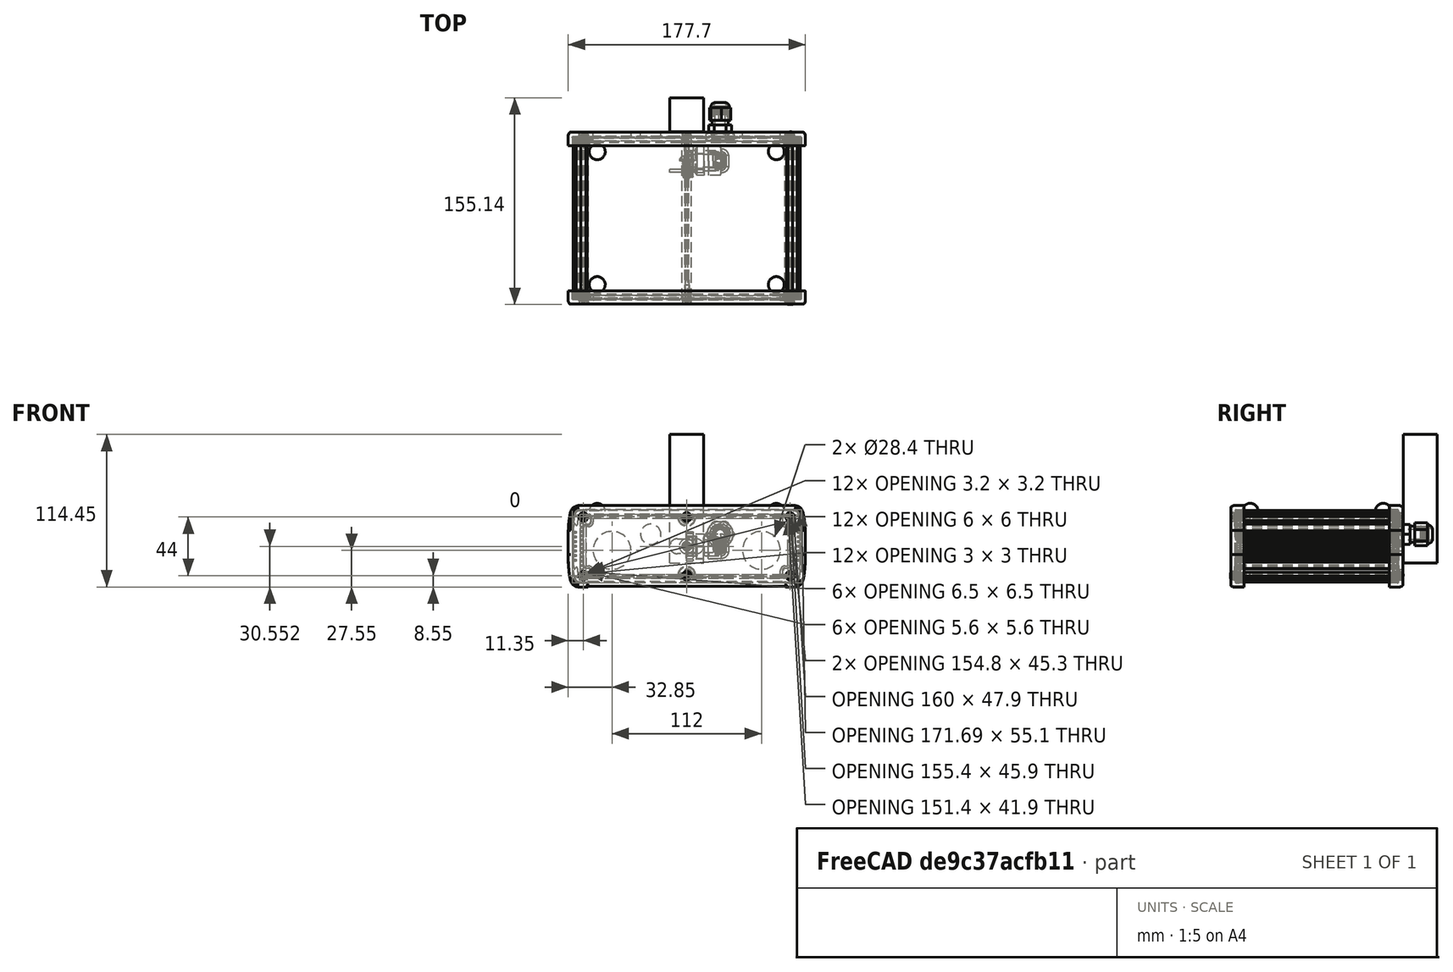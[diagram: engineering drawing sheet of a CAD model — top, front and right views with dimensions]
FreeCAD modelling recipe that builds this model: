
FCSTD DOCUMENT  (FreeCAD 0.19R24276 (Git))
Label: polyCaseCutOuts
License: All rights reserved
LicenseURL: http://en.wikipedia.org/wiki/All_rights_reserved
objects: Part::Feature×27, TechDraw::DrawViewDimension×25, Part::Cylinder×5, Part::Compound2×4, Part::Box×1, Part::MultiFuse×1, Part::Cut×1, TechDraw::DrawSVGTemplate×1, TechDraw::DrawViewPart×1, TechDraw::DrawPage×1
note: 35 computed .brp shape members not serialized (recipe doc carries the construction recipe); baked Part::Feature solids carry a one-line shape summary decoded from their .brp

FEATURE [Part::Feature] Feature  label="EX-64-002"
  Placement = pos=(0,-43,1e-14) rot=(0,0.707107,-0.707107;3.14159rad)
  shape: bbox 178.8 x 129.6 x 63.35 mm, 1628 faces, 33 solids (baked)
FEATURE [Part::Feature] Shell020
  shape: bbox 36.98 x 18.12 x 36.6 mm, 205 faces, 0 solids (baked)
FEATURE [Part::Feature] Shell021
  shape: bbox 36.98 x 21.68 x 36.68 mm, 152 faces, 0 solids (baked)
FEATURE [Part::Feature] Shell022
  shape: bbox 22.66 x 11.43 x 22.66 mm, 6 faces, 0 solids (baked)
FEATURE [Part::Feature] Shell023
  shape: bbox 24.46 x 14.2 x 24.46 mm, 102 faces, 0 solids (baked)
FEATURE [Part::Feature] Shell024
  shape: bbox 35.58 x 29.16 x 35.58 mm, 49 faces, 0 solids (baked)
FEATURE [Part::Feature] Shell025
  shape: bbox 0.2577 x 0.3048 x 0.4459 mm, 1 faces, 0 solids (baked)
FEATURE [Part::Feature] Shell026
  shape: bbox 0.3892 x 1.194 x 0.6742 mm, 1 faces, 0 solids (baked)
FEATURE [Part::Feature] Shell027
  shape: bbox 0.3612 x 0.889 x 0.6255 mm, 1 faces, 0 solids (baked)
FEATURE [Part::Feature] Shell028
  shape: bbox 0.2703 x 0.381 x 0.4682 mm, 1 faces, 0 solids (baked)
FEATURE [Part::Compound2] Compound001  label="M3222GBH_SW0001"
  Links = -> [Shell020,Shell021,Shell022,Shell023,Shell024,Shell025,Shell026,Shell027,Shell028]
  Placement = pos=(-56,9,-3) rot=(0,0,1;0rad)
FEATURE [Part::Feature] Solid003
  shape: bbox 15.45 x 36 x 21.9 mm, 27 faces (baked)
FEATURE [Part::Feature] Solid004
  shape: bbox 29.5 x 21.9 x 19 mm, 79 faces (baked)
FEATURE [Part::Feature] Solid002
  shape: bbox 1 x 19 x 19 mm, 6 faces (baked)
FEATURE [Part::Feature] Solid005
  shape: bbox 5.2 x 24 x 22.95 mm, 27 faces (baked)
FEATURE [Part::Feature] Solid001
  shape: bbox 8 x 12 x 12 mm, 6 faces (baked)
FEATURE [Part::Compound2] Compound002  label="PG9"
  Links = -> [Solid004,Solid001,Solid002,Solid003,Solid005]
  Placement = pos=(-27,14,9) rot=(0,0,1;1.5708rad)
FEATURE [Part::Box] Box  label="tSlotLog"
  AttacherType = Attacher::AttachEngine3D
  Height = 96.4
  Length = 25.4
  Placement = pos=(-12.7,22,-12.5) rot=(0,0,1;0rad)
  Width = 25.4
FEATURE [Part::Feature] Feature001  label="PG7"
  Placement = pos=(25,27,9) rot=(1,0,0;1.5708rad)
  shape: bbox 21.32 x 29.79 x 20.97 mm, 246 faces, 3 solids (baked)
FEATURE [Part::Feature] Shell029
  shape: bbox 36.98 x 21.68 x 36.68 mm, 152 faces, 0 solids (baked)
FEATURE [Part::Feature] Shell030
  shape: bbox 22.66 x 11.43 x 22.66 mm, 6 faces, 0 solids (baked)
FEATURE [Part::Feature] Shell031
  shape: bbox 0.3612 x 0.889 x 0.6255 mm, 1 faces, 0 solids (baked)
FEATURE [Part::Feature] Shell032
  shape: bbox 35.58 x 29.16 x 35.58 mm, 49 faces, 0 solids (baked)
FEATURE [Part::Feature] Shell033
  shape: bbox 24.46 x 14.2 x 24.46 mm, 102 faces, 0 solids (baked)
FEATURE [Part::Feature] Shell034
  shape: bbox 0.3892 x 1.194 x 0.6742 mm, 1 faces, 0 solids (baked)
FEATURE [Part::Feature] Shell035
  shape: bbox 0.2703 x 0.381 x 0.4682 mm, 1 faces, 0 solids (baked)
FEATURE [Part::Feature] Shell036
  shape: bbox 0.2577 x 0.3048 x 0.4459 mm, 1 faces, 0 solids (baked)
FEATURE [Part::Feature] Shell037
  shape: bbox 36.98 x 18.12 x 36.6 mm, 205 faces, 0 solids (baked)
FEATURE [Part::Compound2] Compound003  label="M3222GBH_SW0002"
  Links = -> [Shell037,Shell029,Shell030,Shell033,Shell032,Shell036,Shell034,Shell031,Shell035]
  Placement = pos=(56,9,-3) rot=(0,0,1;0rad)
FEATURE [Part::Feature] Solid
  shape: bbox 11.1 x 17.44 x 11.1 mm, 45 faces (baked)
FEATURE [Part::Feature] Solid006
  shape: bbox 25.4 x 3.15 x 11.25 mm, 11 faces (baked)
FEATURE [Part::Compound2] Compound  label="47065T139_T-Slotted Framing"
  Links = -> [Solid,Solid006]
  Placement = pos=(-2.4e-15,15,0) rot=(-0.707107,0,0.707107;3.14159rad)
FEATURE [Part::Cylinder] Cylinder  label="tSlotCut"
  Angle = 360
  AttacherType = Attacher::AttachEngine3D
  Height = 20
  Placement = pos=(0,9,0) rot=(-1,0,0;1.5708rad)
  Radius = 3.2
FEATURE [Part::Cylinder] Cylinder001  label="M3222GBH_SW0001_Cut"
  Angle = 360
  AttacherType = Attacher::AttachEngine3D
  Height = 50
  Placement = pos=(-56,-5,-3) rot=(-1,0,0;1.5708rad)
  Radius = 14.2
FEATURE [Part::Cylinder] Cylinder002  label="M3222GBH_SW0001_Cut001"
  Angle = 360
  AttacherType = Attacher::AttachEngine3D
  Height = 50
  Placement = pos=(56,-5,-3) rot=(-1,0,0;1.5708rad)
  Radius = 14.2
FEATURE [Part::Cylinder] Cylinder003  label="PG9Cut"
  Angle = 360
  AttacherType = Attacher::AttachEngine3D
  Height = 20
  Placement = pos=(-27,9,9) rot=(-1,0,0;1.5708rad)
  Radius = 7.6
FEATURE [Part::Cylinder] Cylinder004  label="PG9Cut001"
  Angle = 360
  AttacherType = Attacher::AttachEngine3D
  Height = 20
  Placement = pos=(25,9,9) rot=(-1,0,0;1.5708rad)
  Radius = 6.2
FEATURE [Part::MultiFuse] Fusion  label="cuts"
  Shapes = -> [Cylinder004,Cylinder003,Cylinder,Cylinder001,Cylinder002]
FEATURE [Part::Cut] Cut  label="Ex-64Cuts"
  Base = -> Feature
  Tool = -> Fusion
FEATURE [TechDraw::DrawSVGTemplate] Template
  EditableTexts = Designed_by_Name=Designed by Name; Drawing_number=Drawing number; FC-Date=Date; FC-SC=Scale; FC-SH=Sheet; FC-Title=Title; Subtitle=Subtitle; Weight=Weight
  Height = 210
  Orientation = 1
  Width = 297
FEATURE [TechDraw::DrawViewPart] View  label="External View"
  CoarseView = false
  Direction = (0,1,0)
  Focus = 100
  HardHidden = false
  IsoCount = 0
  IsoHidden = false
  IsoVisible = false
  LockPosition = false
  Perspective = false
  Rotation = 0
  ScaleType = 0
  SeamHidden = false
  SeamVisible = true
  SmoothHidden = false
  SmoothVisible = true
  Source = -> [Cut]
  X = 135.756
  XDirection = (-1,0,0)
  Y = 134.867
FEATURE [TechDraw::DrawViewDimension] Dimension002
  Arbitrary = false
  ArbitraryTolerances = false
  EqualTolerance = true
  FormatSpec = ⌀%.2f
  FormatSpecOverTolerance = %+.2f
  FormatSpecUnderTolerance = %+.2f
  Inverted = false
  LockPosition = false
  MeasureType = 1
  OverTolerance = 0
  References2D = -> [View]
  Rotation = 0
  ScaleType = 0
  TheoreticalExact = false
  Type = 5
  UnderTolerance = 0
  X = -26.8003
  Y = 11.2115
FEATURE [TechDraw::DrawViewDimension] Dimension001
  Arbitrary = false
  ArbitraryTolerances = false
  EqualTolerance = true
  FormatSpec = ⌀%.2f
  FormatSpecOverTolerance = %+.2f
  FormatSpecUnderTolerance = %+.2f
  Inverted = false
  LockPosition = false
  MeasureType = 1
  OverTolerance = 0
  References2D = -> [View]
  Rotation = 0
  ScaleType = 0
  TheoreticalExact = false
  Type = 5
  UnderTolerance = 0
  X = -53.3802
  Y = 0.342317
FEATURE [TechDraw::DrawViewDimension] Dimension
  Arbitrary = false
  ArbitraryTolerances = false
  EqualTolerance = true
  FormatSpec = %.2f
  FormatSpecOverTolerance = %+.2f
  FormatSpecUnderTolerance = %+.2f
  Inverted = false
  LockPosition = false
  MeasureType = 1
  OverTolerance = 0
  References2D = -> [View]
  Rotation = 0
  ScaleType = 0
  TheoreticalExact = false
  Type = 1
  UnderTolerance = 0
  X = 7.11e-14
  Y = -30.5235
FEATURE [TechDraw::DrawViewDimension] Dimension004
  Arbitrary = false
  ArbitraryTolerances = false
  EqualTolerance = true
  FormatSpec = ⌀%.2f
  FormatSpecOverTolerance = %+.2f
  FormatSpecUnderTolerance = %+.2f
  Inverted = false
  LockPosition = false
  MeasureType = 1
  OverTolerance = 0
  References2D = -> [View]
  Rotation = 0
  ScaleType = 0
  TheoreticalExact = false
  Type = 5
  UnderTolerance = 0
  X = 29.4596
  Y = 12.3737
FEATURE [TechDraw::DrawViewDimension] Dimension005
  Arbitrary = false
  ArbitraryTolerances = false
  EqualTolerance = true
  FormatSpec = ⌀%.2f
  FormatSpecOverTolerance = %+.2f
  FormatSpecUnderTolerance = %+.2f
  Inverted = false
  LockPosition = false
  MeasureType = 1
  OverTolerance = 0
  References2D = -> [View]
  Rotation = 0
  ScaleType = 0
  TheoreticalExact = false
  Type = 5
  UnderTolerance = 0
  X = 60.4786
  Y = 0.493887
FEATURE [TechDraw::DrawViewDimension] Dimension009
  Arbitrary = false
  ArbitraryTolerances = false
  EqualTolerance = true
  FormatSpec = %.2f
  FormatSpecOverTolerance = %+.2f
  FormatSpecUnderTolerance = %+.2f
  Inverted = false
  LockPosition = false
  MeasureType = 1
  OverTolerance = 0
  References2D = -> [View]
  Rotation = 0
  ScaleType = 0
  TheoreticalExact = false
  Type = 2
  UnderTolerance = 0
  X = -59.3059
  Y = 20.4711
FEATURE [TechDraw::DrawViewDimension] Dimension003
  Arbitrary = false
  ArbitraryTolerances = false
  EqualTolerance = true
  FormatSpec = ⌀%.2f
  FormatSpecOverTolerance = %+.2f
  FormatSpecUnderTolerance = %+.2f
  Inverted = false
  LockPosition = false
  MeasureType = 1
  OverTolerance = 0
  References2D = -> [View]
  Rotation = 0
  ScaleType = 0
  TheoreticalExact = false
  Type = 5
  UnderTolerance = 0
  X = 8.56795
  Y = 3.56177
FEATURE [TechDraw::DrawViewDimension] Dimension010
  Arbitrary = false
  ArbitraryTolerances = false
  EqualTolerance = true
  FormatSpec = %.2f
  FormatSpecOverTolerance = %+.2f
  FormatSpecUnderTolerance = %+.2f
  Inverted = false
  LockPosition = false
  MeasureType = 1
  OverTolerance = 0
  References2D = -> [View]
  Rotation = 0
  ScaleType = 0
  TheoreticalExact = false
  Type = 1
  UnderTolerance = 0
  X = -79.7934
  Y = 0.297386
FEATURE [TechDraw::DrawViewDimension] Dimension011
  Arbitrary = false
  ArbitraryTolerances = false
  EqualTolerance = true
  FormatSpec = %.2f
  FormatSpecOverTolerance = %+.2f
  FormatSpecUnderTolerance = %+.2f
  Inverted = false
  LockPosition = false
  MeasureType = 1
  OverTolerance = 0
  References2D = -> [View]
  Rotation = 0
  ScaleType = 0
  TheoreticalExact = false
  Type = 2
  UnderTolerance = 0
  X = -57.5045
  Y = -22.196
FEATURE [TechDraw::DrawViewDimension] Dimension012
  Arbitrary = false
  ArbitraryTolerances = false
  EqualTolerance = true
  FormatSpec = %.2f
  FormatSpecOverTolerance = %+.2f
  FormatSpecUnderTolerance = %+.2f
  Inverted = false
  LockPosition = false
  MeasureType = 1
  OverTolerance = 0
  References2D = -> [View]
  Rotation = 0
  ScaleType = 0
  TheoreticalExact = false
  Type = 2
  UnderTolerance = 0
  X = -26.9248
  Y = 24.0346
FEATURE [TechDraw::DrawViewDimension] Dimension013
  Arbitrary = false
  ArbitraryTolerances = false
  EqualTolerance = true
  FormatSpec = %.2f
  FormatSpecOverTolerance = %+.2f
  FormatSpecUnderTolerance = %+.2f
  Inverted = false
  LockPosition = false
  MeasureType = 1
  OverTolerance = 0
  References2D = -> [View]
  Rotation = 0
  ScaleType = 0
  TheoreticalExact = false
  Type = 2
  UnderTolerance = 0
  X = 22.4977
  Y = 25.2623
FEATURE [TechDraw::DrawViewDimension] Dimension014
  Arbitrary = false
  ArbitraryTolerances = false
  EqualTolerance = true
  FormatSpec = %.2f
  FormatSpecOverTolerance = %+.2f
  FormatSpecUnderTolerance = %+.2f
  Inverted = false
  LockPosition = false
  MeasureType = 1
  OverTolerance = 0
  References2D = -> [View]
  Rotation = 0
  ScaleType = 0
  TheoreticalExact = false
  Type = 2
  UnderTolerance = 0
  X = 52.8053
  Y = 21.0418
FEATURE [TechDraw::DrawViewDimension] Dimension015
  Arbitrary = false
  ArbitraryTolerances = false
  EqualTolerance = true
  FormatSpec = %.2f
  FormatSpecOverTolerance = %+.2f
  FormatSpecUnderTolerance = %+.2f
  Inverted = false
  LockPosition = false
  MeasureType = 1
  OverTolerance = 0
  References2D = -> [View]
  Rotation = 0
  ScaleType = 0
  TheoreticalExact = false
  Type = 1
  UnderTolerance = 0
  X = 78.3597
  Y = 2.50131
FEATURE [TechDraw::DrawViewDimension] Dimension016
  Arbitrary = false
  ArbitraryTolerances = false
  EqualTolerance = true
  FormatSpec = %.2f
  FormatSpecOverTolerance = %+.2f
  FormatSpecUnderTolerance = %+.2f
  Inverted = false
  LockPosition = false
  MeasureType = 1
  OverTolerance = 0
  References2D = -> [View]
  Rotation = 0
  ScaleType = 0
  TheoreticalExact = false
  Type = 2
  UnderTolerance = 0
  X = 53.3164
  Y = -21.4677
FEATURE [TechDraw::DrawViewDimension] Dimension017
  Arbitrary = false
  ArbitraryTolerances = false
  EqualTolerance = true
  FormatSpec = %.2f
  FormatSpecOverTolerance = %+.2f
  FormatSpecUnderTolerance = %+.2f
  Inverted = false
  LockPosition = false
  MeasureType = 1
  OverTolerance = 0
  References2D = -> [View]
  Rotation = 0
  ScaleType = 0
  TheoreticalExact = false
  Type = 1
  UnderTolerance = 0
  X = -60.9532
  Y = 5.48366
FEATURE [TechDraw::DrawViewDimension] Dimension018
  Arbitrary = false
  ArbitraryTolerances = false
  EqualTolerance = true
  FormatSpec = %.2f
  FormatSpecOverTolerance = %+.2f
  FormatSpecUnderTolerance = %+.2f
  Inverted = false
  LockPosition = false
  MeasureType = 1
  OverTolerance = 0
  References2D = -> [View]
  Rotation = 0
  ScaleType = 0
  TheoreticalExact = false
  Type = 1
  UnderTolerance = 0
  X = 17.0933
  Y = -2.49522
FEATURE [TechDraw::DrawViewDimension] Dimension019
  Arbitrary = false
  ArbitraryTolerances = false
  EqualTolerance = true
  FormatSpec = %.2f
  FormatSpecOverTolerance = %+.2f
  FormatSpecUnderTolerance = %+.2f
  Inverted = false
  LockPosition = false
  MeasureType = 1
  OverTolerance = 0
  References2D = -> [View]
  Rotation = 0
  ScaleType = 0
  TheoreticalExact = false
  Type = 2
  UnderTolerance = 0
  X = -28.1319
  Y = -12.4515
FEATURE [TechDraw::DrawViewDimension] Dimension020
  Arbitrary = false
  ArbitraryTolerances = false
  EqualTolerance = true
  FormatSpec = %.2f
  FormatSpecOverTolerance = %+.2f
  FormatSpecUnderTolerance = %+.2f
  Inverted = false
  LockPosition = false
  MeasureType = 1
  OverTolerance = 0
  References2D = -> [View]
  Rotation = 0
  ScaleType = 0
  TheoreticalExact = false
  Type = 1
  UnderTolerance = 0
  X = 25.0729
  Y = -6.69401
FEATURE [TechDraw::DrawViewDimension] Dimension021
  Arbitrary = false
  ArbitraryTolerances = false
  EqualTolerance = true
  FormatSpec = %.2f
  FormatSpecOverTolerance = %+.2f
  FormatSpecUnderTolerance = %+.2f
  Inverted = false
  LockPosition = false
  MeasureType = 1
  OverTolerance = 0
  References2D = -> [View]
  Rotation = 0
  ScaleType = 0
  TheoreticalExact = false
  Type = 2
  UnderTolerance = 0
  X = -6.99932
  Y = -13.6516
FEATURE [TechDraw::DrawViewDimension] Dimension022
  Arbitrary = false
  ArbitraryTolerances = false
  EqualTolerance = true
  FormatSpec = %.2f
  FormatSpecOverTolerance = %+.2f
  FormatSpecUnderTolerance = %+.2f
  Inverted = false
  LockPosition = false
  MeasureType = 1
  OverTolerance = 0
  References2D = -> [View]
  Rotation = 0
  ScaleType = 0
  TheoreticalExact = false
  Type = 2
  UnderTolerance = 0
  X = -9.15587
  Y = 20.4863
FEATURE [TechDraw::DrawViewDimension] Dimension023
  Arbitrary = false
  ArbitraryTolerances = false
  EqualTolerance = true
  FormatSpec = %.2f
  FormatSpecOverTolerance = %+.2f
  FormatSpecUnderTolerance = %+.2f
  Inverted = false
  LockPosition = false
  MeasureType = 1
  OverTolerance = 0
  References2D = -> [View]
  Rotation = 0
  ScaleType = 0
  TheoreticalExact = false
  Type = 1
  UnderTolerance = 0
  X = -43.0308
  Y = 9.91992
FEATURE [TechDraw::DrawViewDimension] Dimension024
  Arbitrary = false
  ArbitraryTolerances = false
  EqualTolerance = true
  FormatSpec = %.2f
  FormatSpecOverTolerance = %+.2f
  FormatSpecUnderTolerance = %+.2f
  Inverted = false
  LockPosition = false
  MeasureType = 1
  OverTolerance = 0
  References2D = -> [View]
  Rotation = 0
  ScaleType = 0
  TheoreticalExact = false
  Type = 1
  UnderTolerance = 0
  X = -41.9951
  Y = 17.0467
FEATURE [TechDraw::DrawViewDimension] Dimension025
  Arbitrary = false
  ArbitraryTolerances = false
  EqualTolerance = true
  FormatSpec = %.2f
  FormatSpecOverTolerance = %+.2f
  FormatSpecUnderTolerance = %+.2f
  Inverted = false
  LockPosition = false
  MeasureType = 1
  OverTolerance = 0
  References2D = -> [View]
  Rotation = 0
  ScaleType = 0
  TheoreticalExact = false
  Type = 1
  UnderTolerance = 0
  X = -42.6156
  Y = 23.097
FEATURE [TechDraw::DrawViewDimension] Dimension026
  Arbitrary = false
  ArbitraryTolerances = false
  EqualTolerance = true
  FormatSpec = %.2f
  FormatSpecOverTolerance = %+.2f
  FormatSpecUnderTolerance = %+.2f
  Inverted = false
  LockPosition = false
  MeasureType = 1
  OverTolerance = 0
  References2D = -> [View]
  Rotation = 0
  ScaleType = 0
  TheoreticalExact = false
  Type = 1
  UnderTolerance = 0
  X = 28.9388
  Y = -11.288
FEATURE [TechDraw::DrawViewDimension] Dimension027
  Arbitrary = false
  ArbitraryTolerances = false
  EqualTolerance = true
  FormatSpec = %.2f
  FormatSpecOverTolerance = %+.2f
  FormatSpecUnderTolerance = %+.2f
  Inverted = false
  LockPosition = false
  MeasureType = 1
  OverTolerance = 0
  References2D = -> [View]
  Rotation = 0
  ScaleType = 0
  TheoreticalExact = false
  Type = 1
  UnderTolerance = 0
  X = 73.1961
  Y = 10.1708
FEATURE [TechDraw::DrawPage] Page
  KeepUpdated = true
  NextBalloonIndex = 1
  ProjectionType = 0
  Template = -> Template
  Views = -> [View,Dimension,Dimension001,Dimension002,Dimension003,Dimension004,Dimension005,Dimension009,Dimension010,Dimension011,Dimension012,Dimension013,Dimension014,Dimension015,Dimension016,Dimension017,Dimension018,Dimension019,Dimension020,Dimension021,Dimension022,Dimension023,Dimension024,Dimension025,Dimension026,Dimension027]
